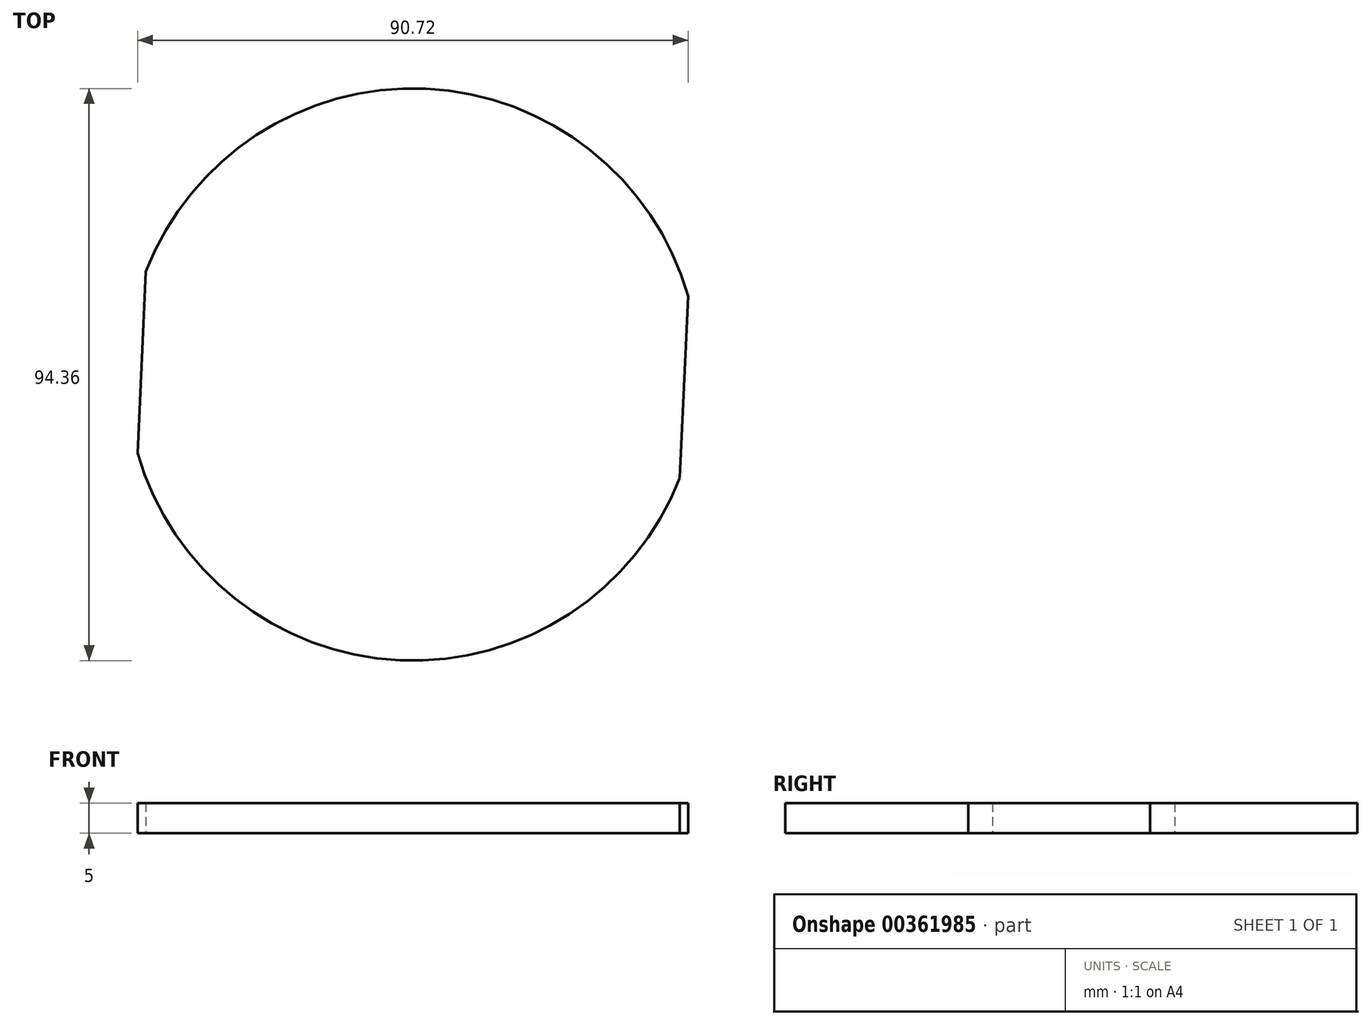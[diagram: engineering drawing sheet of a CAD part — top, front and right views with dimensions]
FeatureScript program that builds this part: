
annotation { "Feature Type Name" : "Feature", "Feature Type Description" : "" }
export const myFeature = defineFeature(function(context is Context, id is Id, definition is map)
    precondition{}
    {
        {
            var Q0;
            Q0=qCreatedBy(makeId("Top.planeOp"),FACE);
            var sketch = newSketch(context, id + "F0", { "sketchPlane" : qUnion([Q0])});
            skCircle(sketch, "E0", {"center": v(0, 0) * mm, "radius": 47.17 * mm});
            skLineSegment(sketch, "E1", {"start": v(-44, 17.01) * mm, "end": v(-45.36, -12.95) * mm});
            skLineSegment(sketch, "E2", {"start": v(45.36, 12.95) * mm, "end": v(44, -17.01) * mm});
            skSolve(sketch);
        }
        {
            var Q0;
            {var subQ0=sQuery(id+"F0.wireOp",EDGE,"E1");Q0=makeQuery(id+"F0.imprint","IMPRINT",FACE,{"disambiguationData":[TD([[makeQuery(id+"F0.imprint","IMPRINT",EDGE,{"derivedFrom":subQ0}),1.0]])]});}
            extrude(context, id + "F1", {"entities" : qUnion([Q0]), "depth" : 5 * mm});
        }
    });
